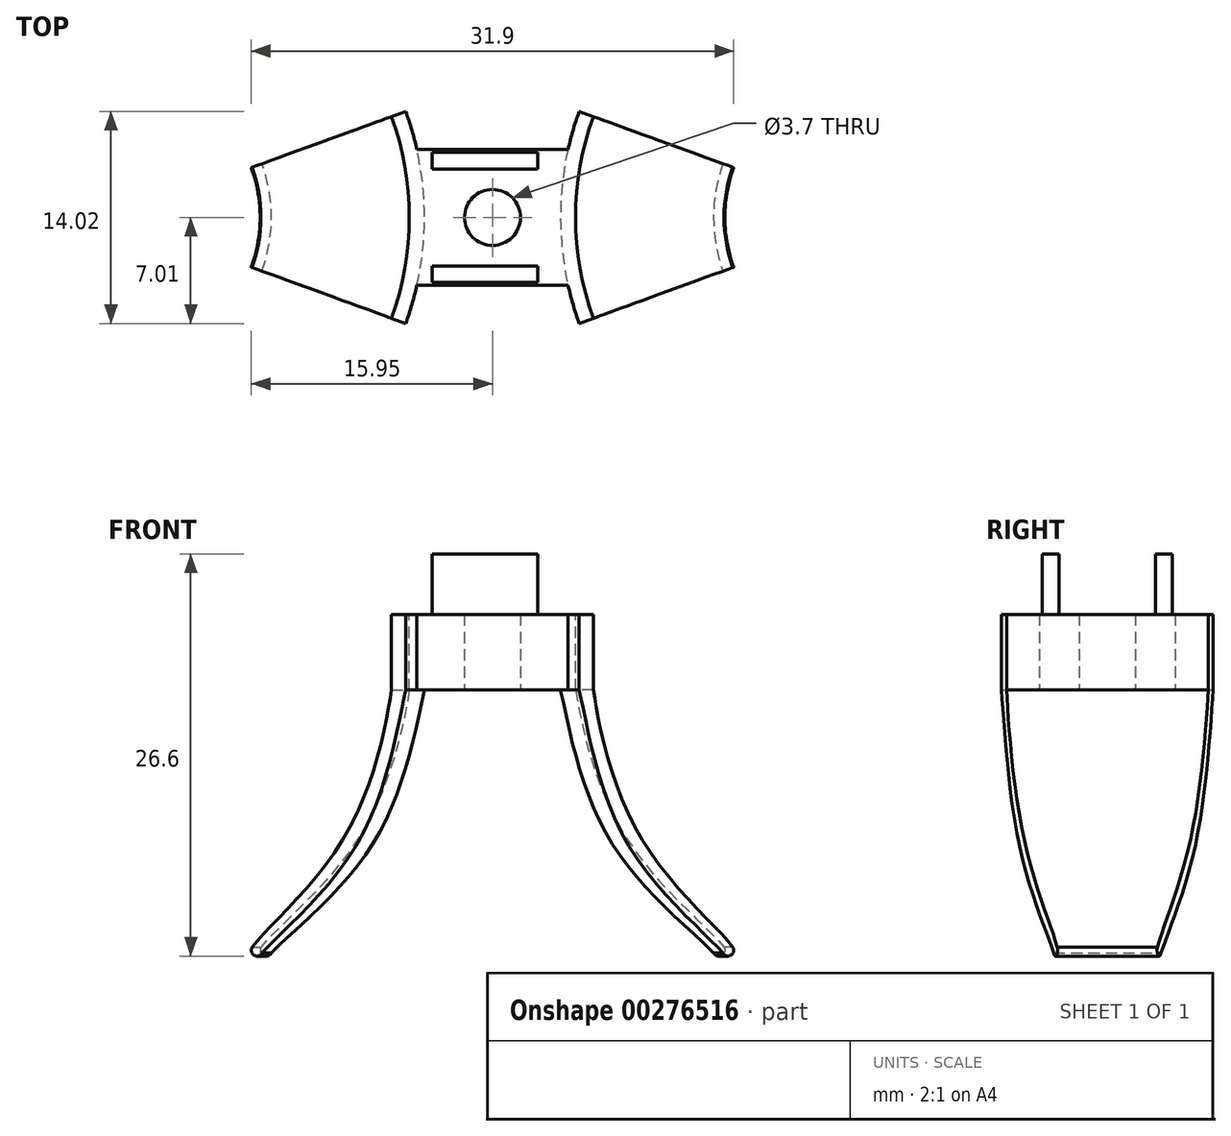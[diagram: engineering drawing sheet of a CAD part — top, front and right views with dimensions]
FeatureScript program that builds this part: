
annotation { "Feature Type Name" : "Feature", "Feature Type Description" : "" }
export const myFeature = defineFeature(function(context is Context, id is Id, definition is map)
    precondition{}
    {
        {
            var Q0;
            Q0=qCreatedBy(makeId("Top.planeOp"),FACE);
            var sketch = newSketch(context, id + "F0", { "sketchPlane" : qUnion([Q0])});
            skLineSegment(sketch, "E0.left", {"start": v(0, 0) * mm, "end": v(0, -9) * mm});
            skLineSegment(sketch, "E0.right", {"start": v(10, 0) * mm, "end": v(10, -9) * mm});
            skLineSegment(sketch, "E1", {"start": v(0, -4.5) * mm, "end": v(10, -4.5) * mm, "construction": true});
            skCircle(sketch, "E2", {"center": v(5, -4.5) * mm, "radius": 1.85 * mm});
            skLineSegment(sketch, "E3", {"start": v(10, -9) * mm, "end": v(0, -9) * mm});
            skLineSegment(sketch, "E4", {"start": v(10, 0) * mm, "end": v(0, 0) * mm});
            skSolve(sketch);
        }
        {
            var Q0;
            Q0=makeQuery(id+"F0.imprint","IMPRINT",FACE,{"disambiguationData":[TD([[makeQuery(id+"F0.imprint","IMPRINT",EDGE,{"derivedFrom":sQuery(id+"F0.wireOp",EDGE,"E0.left")}),1.0]])]});
            extrude(context, id + "F1", {"entities" : qUnion([Q0]), "depth" : 5 * mm});
        }
        {
            var Q0;
            Q0=makeQuery(id+"F1.opExtrude","SWEPT_FACE",FACE,{"disambiguationData":[OSD([sQuery(id+"F0.wireOp",EDGE,"E3")])]});
            cPlane(context, id + "F2", {"entities" : qUnion([Q0]), "cplaneType" : CPlaneType.OFFSET, "offset" : 4.5 * mm, "oppositeDirection" : true, "width" : 150 * mm, "height" : 150 * mm});
        }
        {
            var Q0;
            Q0=qCreatedBy(id+"F2.planeOp",FACE);
            var sketch = newSketch(context, id + "F3", { "sketchPlane" : qUnion([Q0])});
            skLineSegment(sketch, "E5.top", {"start": v(0, 5) * mm, "end": v(-0.5, 5) * mm});
            skLineSegment(sketch, "E5.right", {"start": v(-0.5, 0) * mm, "end": v(-0.5, 5) * mm});
            skLineSegment(sketch, "E6", {"start": v(-0.5, 0) * mm, "end": v(-10.31, -17) * mm, "construction": true});
            skLineSegment(sketch, "E7", {"start": v(-5.4, -8.5) * mm, "end": v(-3.68, -9.5) * mm, "construction": true});
            skFitSpline(sketch, "E8", {"points": [v(-0.5, 0) * mm, v(-3.68, -9.5) * mm, v(-10.31, -17) * mm], "startDerivative": vector(-1.76, -11.23) * mm, "endDerivative": vector(-7.24, -8.77) * mm});
            skLineSegment(sketch, "E9", {"start": v(-3.68, -9.5) * mm, "end": v(-2.8, -10) * mm, "construction": true});
            skLineSegment(sketch, "E10", {"start": v(-10.31, -17) * mm, "end": v(-9.62, -17.4) * mm, "construction": true});
            skArc(sketch, "E11", {"start": v(-10.31, -17) * mm, "mid": v(-10.17, -17.55) * mm, "end": v(-9.62, -17.4) * mm});
            skPoint(sketch, "E11.third.point", {"position": v(-9.62, -17) * mm});
            skFitSpline(sketch, "E12", {"points": [v(-9.62, -17.4) * mm, v(-2.8, -10) * mm, v(0.5, 0) * mm], "startDerivative": vector(7.81, 8.57) * mm, "endDerivative": vector(2.94, 11.98) * mm});
            skLineSegment(sketch, "E13", {"start": v(0.5, 0) * mm, "end": v(0.5, 5) * mm});
            skLineSegment(sketch, "E14", {"start": v(0.5, 5) * mm, "end": v(0, 5) * mm});
            skSolve(sketch);
        }
        {
            var Q0;
            Q0=qCreatedBy(id+"F2.planeOp",FACE);
            var sketch = newSketch(context, id + "F4", { "sketchPlane" : qUnion([Q0])});
            skLineSegment(sketch, "E15", {"start": v(0, 2.5) * mm, "end": v(-20, 2.5) * mm, "construction": true});
            skLineSegment(sketch, "E16", {"start": v(-20, 2.5) * mm, "end": v(-20, 0.36) * mm, "construction": true});
            skSolve(sketch);
        }
        {
            var Q0;
            Q0=qSketchRegion(id+"F3",true);
            var Q1;
            Q1=sQuery(id+"F4.wireOp",EDGE,"E16");
            revolve(context, id + "F5", {"entities" : qUnion([Q0]), "axis" : qUnion([Q1]), "revolveType" : RevolveType.TWO_DIRECTIONS, "angle" : 20 * degree, "angleBack" : 340 * degree});
        }
        {
            var Q0;
            Q0=makeQuery(id+"F5.boolean.opBoolean","MERGE",FACE,{"derivedFrom":[makeQuery(id+"F1.opExtrude","CAP_FACE",FACE,{"disambiguationData":[OSD([sQuery(id+"F0.wireOp",EDGE,"E0.left"),sQuery(id+"F0.wireOp",EDGE,"E0.right"),sQuery(id+"F0.wireOp",EDGE,"E2"),sQuery(id+"F0.wireOp",EDGE,"E3"),sQuery(id+"F0.wireOp",EDGE,"E4")])],"isStart":false}),makeQuery(id+"F5.opRevolve","SWEPT_FACE",FACE,{"disambiguationData":[OSD([sQuery(id+"F3.wireOp",EDGE,"E5.top"),sQuery(id+"F3.wireOp",EDGE,"E14")])]})]});
            var sketch = newSketch(context, id + "F6", { "sketchPlane" : qUnion([Q0])});
            skLineSegment(sketch, "E17.bottom", {"start": v(1, -9) * mm, "end": v(8, -9) * mm});
            skLineSegment(sketch, "E17.top", {"start": v(1, -7.5) * mm, "end": v(8, -7.5) * mm});
            skLineSegment(sketch, "E17.left", {"start": v(1, -9) * mm, "end": v(1, -7.5) * mm});
            skLineSegment(sketch, "E17.right", {"start": v(8, -9) * mm, "end": v(8, -7.5) * mm});
            skCircle(sketch, "E18.0", {"center": v(5, -4.5) * mm, "radius": 1.85 * mm, "construction": true});
            skLineSegment(sketch, "E19.MirrorCS", {"start": v(1, 0) * mm, "end": v(8, 0) * mm});
            skLineSegment(sketch, "E20.MirrorCS", {"start": v(8, 0) * mm, "end": v(8, -1.5) * mm});
            skLineSegment(sketch, "E21.MirrorCS", {"start": v(1, -1.5) * mm, "end": v(8, -1.5) * mm});
            skLineSegment(sketch, "E22.MirrorCS", {"start": v(1, 0) * mm, "end": v(1, -1.5) * mm});
            skSolve(sketch);
        }
        {
            var Q0;
            Q0=makeQuery(id+"F6.imprint","IMPRINT",FACE,{"disambiguationData":[TD([[makeQuery(id+"F6.imprint","IMPRINT",EDGE,{"derivedFrom":sQuery(id+"F6.wireOp",EDGE,"E17.bottom")}),-1.0]])]});
            var Q1;
            Q1=makeQuery(id+"F6.imprint","IMPRINT",FACE,{"disambiguationData":[TD([[makeQuery(id+"F6.imprint","IMPRINT",EDGE,{"derivedFrom":sQuery(id+"F6.wireOp",EDGE,"E19.MirrorCS")}),1.0]])]});
            extrude(context, id + "F7", {"entities" : qUnion([Q0, Q1]), "operationType" : NewBodyOperationType.ADD, "depth" : 4 * mm});
        }
        {
            var Q0;
            Q0=makeQuery(id+"F1.opExtrude","SWEPT_FACE",FACE,{"disambiguationData":[OSD([sQuery(id+"F0.wireOp",EDGE,"E0.right")])]});
            var sketch = newSketch(context, id + "F8", { "sketchPlane" : qUnion([Q0])});
            skLineSegment(sketch, "E23", {"start": v(-7.5, 5) * mm, "end": v(-7.7, 5) * mm});
            skLineSegment(sketch, "E24", {"start": v(-7.7, 5) * mm, "end": v(-7.7, 9) * mm});
            skLineSegment(sketch, "E25.0", {"start": v(-7.5, 9) * mm, "end": v(-7.7, 9) * mm});
            skLineSegment(sketch, "E26", {"start": v(-8.25, 9) * mm, "end": v(-8.25, 6) * mm, "construction": true});
            skLineSegment(sketch, "E27.MirrorCS", {"start": v(-8.8, 5) * mm, "end": v(-8.8, 9) * mm});
            skLineSegment(sketch, "E28.MirrorCS", {"start": v(-9, 5) * mm, "end": v(-8.8, 5) * mm});
            skLineSegment(sketch, "E29.0", {"start": v(-7.5, 9) * mm, "end": v(-7.5, 5) * mm});
            skLineSegment(sketch, "E30.0", {"start": v(-9, 9) * mm, "end": v(-9, 5) * mm});
            skPoint(sketch, "E31.orphan", {"position": v(-9, 0) * mm});
            skLineSegment(sketch, "E32.trimOffspring", {"start": v(-8.8, 9) * mm, "end": v(-9, 9) * mm});
            skLineSegment(sketch, "E33.MirrorCS", {"start": v(-9, 9) * mm, "end": v(-8.8, 9) * mm});
            skLineSegment(sketch, "E34.MirrorCS", {"start": v(-7.7, 9) * mm, "end": v(-7.5, 9) * mm});
            skLineSegment(sketch, "E35", {"start": v(-4.5, 5) * mm, "end": v(-4.5, 7.43) * mm, "construction": true});
            skLineSegment(sketch, "E36.MirrorCS", {"start": v(-0.2, 9) * mm, "end": v(0, 9) * mm});
            skLineSegment(sketch, "E37.MirrorCS", {"start": v(0, 5) * mm, "end": v(-0.2, 5) * mm});
            skLineSegment(sketch, "E38.MirrorCS", {"start": v(0, 9) * mm, "end": v(0, 5) * mm});
            skLineSegment(sketch, "E39.MirrorCS", {"start": v(-0.2, 5) * mm, "end": v(-0.2, 9) * mm});
            skLineSegment(sketch, "E40.MirrorCS", {"start": v(-1.5, 9) * mm, "end": v(-1.3, 9) * mm});
            skLineSegment(sketch, "E41.MirrorCS", {"start": v(-1.5, 9) * mm, "end": v(-1.5, 5) * mm});
            skLineSegment(sketch, "E42.MirrorCS", {"start": v(-1.3, 5) * mm, "end": v(-1.3, 9) * mm});
            skLineSegment(sketch, "E43.MirrorCS", {"start": v(-1.5, 5) * mm, "end": v(-1.3, 5) * mm});
            skSolve(sketch);
        }
        {
            var Q0;
            Q0=qSketchRegion(id+"F8",true);
            extrude(context, id + "F9", {"entities" : qUnion([Q0]), "operationType" : NewBodyOperationType.REMOVE, "oppositeDirection" : true, "depth" : 25 * mm});
        }
        {
            var Q0;
            Q0=makeQuery(id+"F5.opRevolve","SWEPT_BODY",BODY,{"disambiguationData":[OSD([sQuery(id+"F3.wireOp",EDGE,"E5.top"),sQuery(id+"F3.wireOp",EDGE,"E5.right"),sQuery(id+"F3.wireOp",EDGE,"E8"),sQuery(id+"F3.wireOp",EDGE,"E11"),sQuery(id+"F3.wireOp",EDGE,"E12"),sQuery(id+"F3.wireOp",EDGE,"E13"),sQuery(id+"F3.wireOp",EDGE,"E14")])]});
            var Q1;
            Q1=makeQuery(id+"F1.opExtrude","SWEPT_FACE",FACE,{"disambiguationData":[OSD([sQuery(id+"F0.wireOp",EDGE,"E2")])]});
            circularPattern(context, id + "F10", {"operationType" : NewBodyOperationType.ADD, "entities" : qUnion([Q0]), "axis" : qUnion([Q1]), "angle" : 360 * degree, "instanceCount" : 2, "equalSpace" : true});
        }
    });
